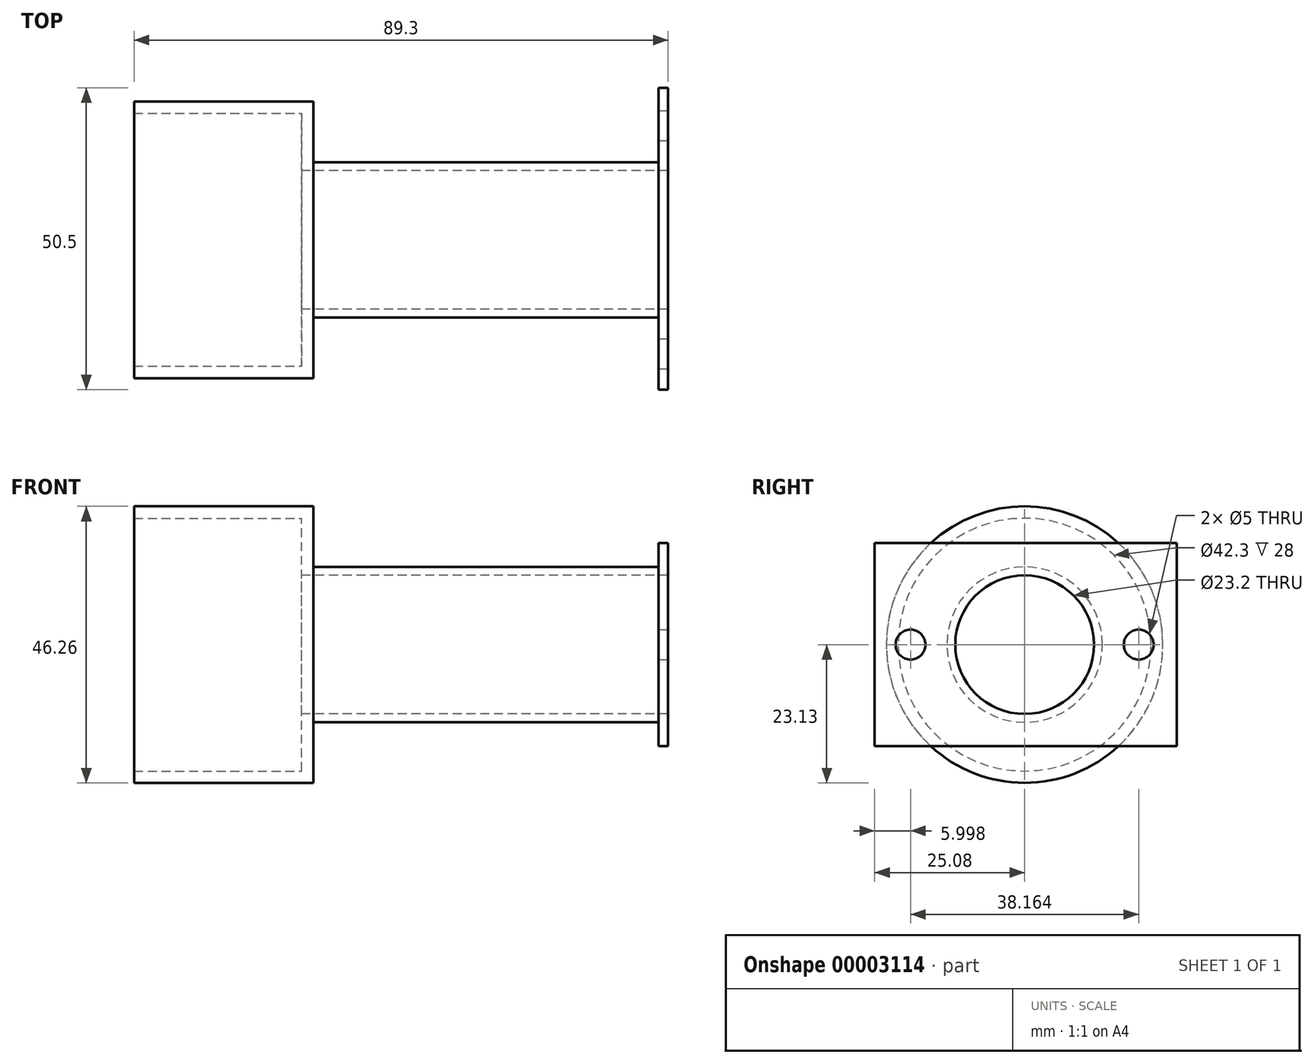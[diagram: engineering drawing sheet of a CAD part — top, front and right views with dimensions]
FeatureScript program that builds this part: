
annotation { "Feature Type Name" : "Feature", "Feature Type Description" : "" }
export const myFeature = defineFeature(function(context is Context, id is Id, definition is map)
    precondition{}
    {
        {
            var Q0;
            Q0=qCreatedBy(makeId("Right.planeOp"),FACE);
            var sketch = newSketch(context, id + "F0", { "sketchPlane" : qUnion([Q0])});
            skCircle(sketch, "E0", {"center": v(0, 0) * mm, "radius": 23.12 * mm});
            skCircle(sketch, "E1", {"center": v(0, 0) * mm, "radius": 21.15 * mm});
            skCircle(sketch, "E2", {"center": v(0, 0) * mm, "radius": 11.6 * mm});
            skSolve(sketch);
        }
        {
            var Q0;
            Q0=makeQuery(id+"F0.imprint","IMPRINT",FACE,{"disambiguationData":[TD([[makeQuery(id+"F0.imprint","IMPRINT",EDGE,{"derivedFrom":sQuery(id+"F0.wireOp",EDGE,"E0")}),1.0]])]});
            extrude(context, id + "F1", {"entities" : qUnion([Q0]), "oppositeDirection" : true, "depth" : 28 * mm});
        }
        {
            var Q0;
            Q0=makeQuery(id+"F0.imprint","IMPRINT",FACE,{"disambiguationData":[TD([[makeQuery(id+"F0.imprint","IMPRINT",EDGE,{"derivedFrom":sQuery(id+"F0.wireOp",EDGE,"E1")}),1.0]])]});
            var Q1;
            Q1=makeQuery(id+"F1.opExtrude","CAP_FACE",FACE,{"disambiguationData":[OSD([sQuery(id+"F0.wireOp",EDGE,"E0"),sQuery(id+"F0.wireOp",EDGE,"E1")])],"isStart":true});
            extrude(context, id + "F2", {"entities" : qUnion([Q0, Q1]), "operationType" : NewBodyOperationType.ADD, "depth" : 2 * mm});
        }
        {
            var Q0;
            {var subQ0=sQuery(id+"F0.wireOp",EDGE,"E1");Q0=makeQuery(id+"F2.boolean.opBoolean","MERGE",FACE,{"derivedFrom":[makeQuery(id+"F2.opExtrude","CAP_FACE",FACE,{"disambiguationData":[OSD([subQ0,sQuery(id+"F0.wireOp",EDGE,"E2")])],"isStart":false}),makeQuery(id+"F2.opExtrude","CAP_FACE",FACE,{"disambiguationData":[OSD([sQuery(id+"F0.wireOp",EDGE,"E0"),subQ0])],"isStart":false})]});}
            var sketch = newSketch(context, id + "F3", { "sketchPlane" : qUnion([Q0])});
            skCircle(sketch, "E3", {"center": v(0, 0) * mm, "radius": 13 * mm});
            skSolve(sketch);
        }
        {
            var Q0;
            Q0=makeQuery(id+"F3.imprint","IMPRINT",FACE,{"disambiguationData":[TD([[makeQuery(id+"F3.imprint","IMPRINT",EDGE,{"derivedFrom":sQuery(id+"F3.wireOp",EDGE,"E3")}),1.0]])]});
            extrude(context, id + "F4", {"entities" : qUnion([Q0]), "operationType" : NewBodyOperationType.ADD, "depth" : 59.3 * mm});
        }
        {
            var Q0;
            Q0=makeQuery(id+"F4.opExtrude","CAP_FACE",FACE,{"disambiguationData":[OSD([sQuery(id+"F0.wireOp",EDGE,"E2"),sQuery(id+"F3.wireOp",EDGE,"E3")])],"isStart":false});
            var sketch = newSketch(context, id + "F5", { "sketchPlane" : qUnion([Q0])});
            skLineSegment(sketch, "E4.bottom", {"start": v(-25.08, 17) * mm, "end": v(25.42, 17) * mm});
            skLineSegment(sketch, "E4.top", {"start": v(-25.08, -17) * mm, "end": v(25.42, -17) * mm});
            skLineSegment(sketch, "E4.left", {"start": v(-25.08, 17) * mm, "end": v(-25.08, -17) * mm});
            skLineSegment(sketch, "E4.right", {"start": v(25.42, 17) * mm, "end": v(25.42, -17) * mm});
            skLineSegment(sketch, "E5", {"start": v(0, 0) * mm, "end": v(18.37, 0) * mm, "construction": true});
            skLineSegment(sketch, "E6", {"start": v(0, 0) * mm, "end": v(0, 7.34) * mm, "construction": true});
            skCircle(sketch, "E7", {"center": v(0, -1.05) * mm, "radius": 19.11 * mm, "construction": true});
            skPoint(sketch, "E8", {"position": v(19.08, 0) * mm});
            skPoint(sketch, "E9", {"position": v(-19.08, 0) * mm});
            skSolve(sketch);
        }
        {
            var Q0;
            Q0=makeQuery(id+"F5.imprint","IMPRINT",FACE,{"disambiguationData":[TD([[makeQuery(id+"F5.imprint","IMPRINT",EDGE,{"derivedFrom":sQuery(id+"F5.wireOp",EDGE,"E4.bottom")}),-1.0]])]});
            extrude(context, id + "F6", {"entities" : qUnion([Q0]), "operationType" : NewBodyOperationType.ADD, "oppositeDirection" : true, "depth" : 1.6 * mm});
        }
        {
            var Q0;
            Q0=sQuery(id+"F5.wireOp",VERTEX,"E9");
            var Q1;
            Q1=sQuery(id+"F5.wireOp",VERTEX,"E8");
            var Q2;
            Q2=makeQuery(id+"F1.opExtrude","SWEPT_BODY",BODY,{"disambiguationData":[OSD([sQuery(id+"F0.wireOp",EDGE,"E0"),sQuery(id+"F0.wireOp",EDGE,"E1")])]});
            hole(context, id + "F7", {"style" : HoleStyle.SIMPLE, "endStyle" : HoleEndStyle.BLIND, "standardTappedOrClearance" : lookupTablePath({ "standard" : "ISO", "size" : "5", "type" : "Drilled" }), "standardBlindInLast" : lookupTablePath({ "standard" : "ISO", "size" : "5", "type" : "Drilled" }), "holeDiameter" : 5 * mm, "holeDepth" : 2 * mm, "tappedDepth" : 2 * mm, "tapClearance" : 3, "startFromSketch" : true, "locations" : qUnion([Q0, Q1]), "scope" : qUnion([Q2])});
        }
    });
